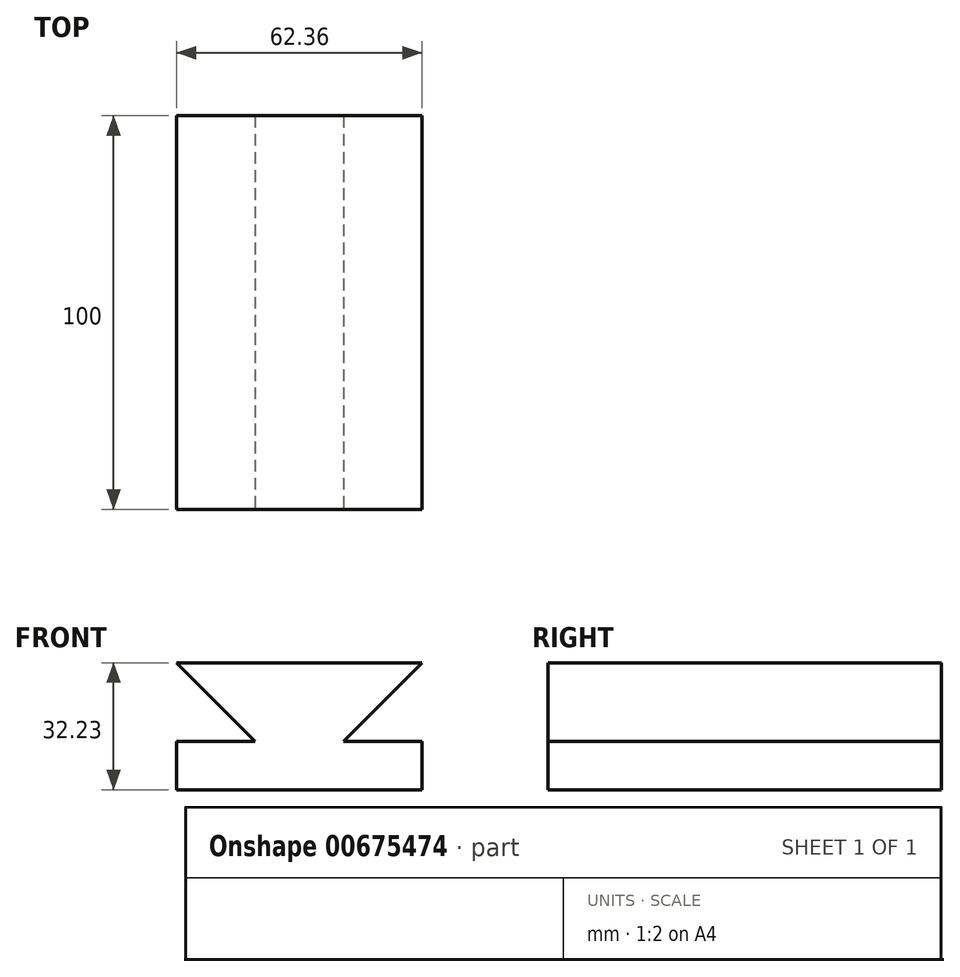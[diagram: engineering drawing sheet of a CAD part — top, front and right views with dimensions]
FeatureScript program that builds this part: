
annotation { "Feature Type Name" : "Feature", "Feature Type Description" : "" }
export const myFeature = defineFeature(function(context is Context, id is Id, definition is map)
    precondition{}
    {
        {
            var Q0;
            Q0=qCreatedBy(makeId("Front.planeOp"),FACE);
            var sketch = newSketch(context, id + "F0", { "sketchPlane" : qUnion([Q0])});
            skLineSegment(sketch, "E0.bottom", {"start": v(-30.56, 6.73) * mm, "end": v(-10.6, 6.73) * mm});
            skLineSegment(sketch, "E0.top", {"start": v(-30.56, -5.56) * mm, "end": v(31.76, -5.56) * mm});
            skLineSegment(sketch, "E0.left", {"start": v(-30.56, 6.73) * mm, "end": v(-30.56, -5.56) * mm});
            skLineSegment(sketch, "E0.right", {"start": v(31.76, 6.73) * mm, "end": v(31.76, -5.56) * mm});
            skLineSegment(sketch, "E1", {"start": v(-30.56, 26.67) * mm, "end": v(-10.6, 6.73) * mm});
            skLineSegment(sketch, "E2.trimOffspring", {"start": v(11.85, 6.73) * mm, "end": v(31.76, 6.73) * mm});
            skPoint(sketch, "E3.end.orphan", {"position": v(31.76, 27.84) * mm});
            skLineSegment(sketch, "E4", {"start": v(-30.56, 26.67) * mm, "end": v(31.8, 26.67) * mm});
            skLineSegment(sketch, "E5", {"start": v(31.8, 26.67) * mm, "end": v(11.85, 6.73) * mm});
            skSolve(sketch);
        }
        {
            var Q0;
            Q0=makeQuery(id+"F0.imprint","IMPRINT",FACE,{"disambiguationData":[TD([[makeQuery(id+"F0.imprint","IMPRINT",EDGE,{"derivedFrom":sQuery(id+"F0.wireOp",EDGE,"E0.bottom")}),-1.0]])]});
            extrude(context, id + "F1", {"entities" : qUnion([Q0]), "oppositeDirection" : true, "depth" : 100 * mm, "offsetDistance" : 25 * mm});
        }
    });
